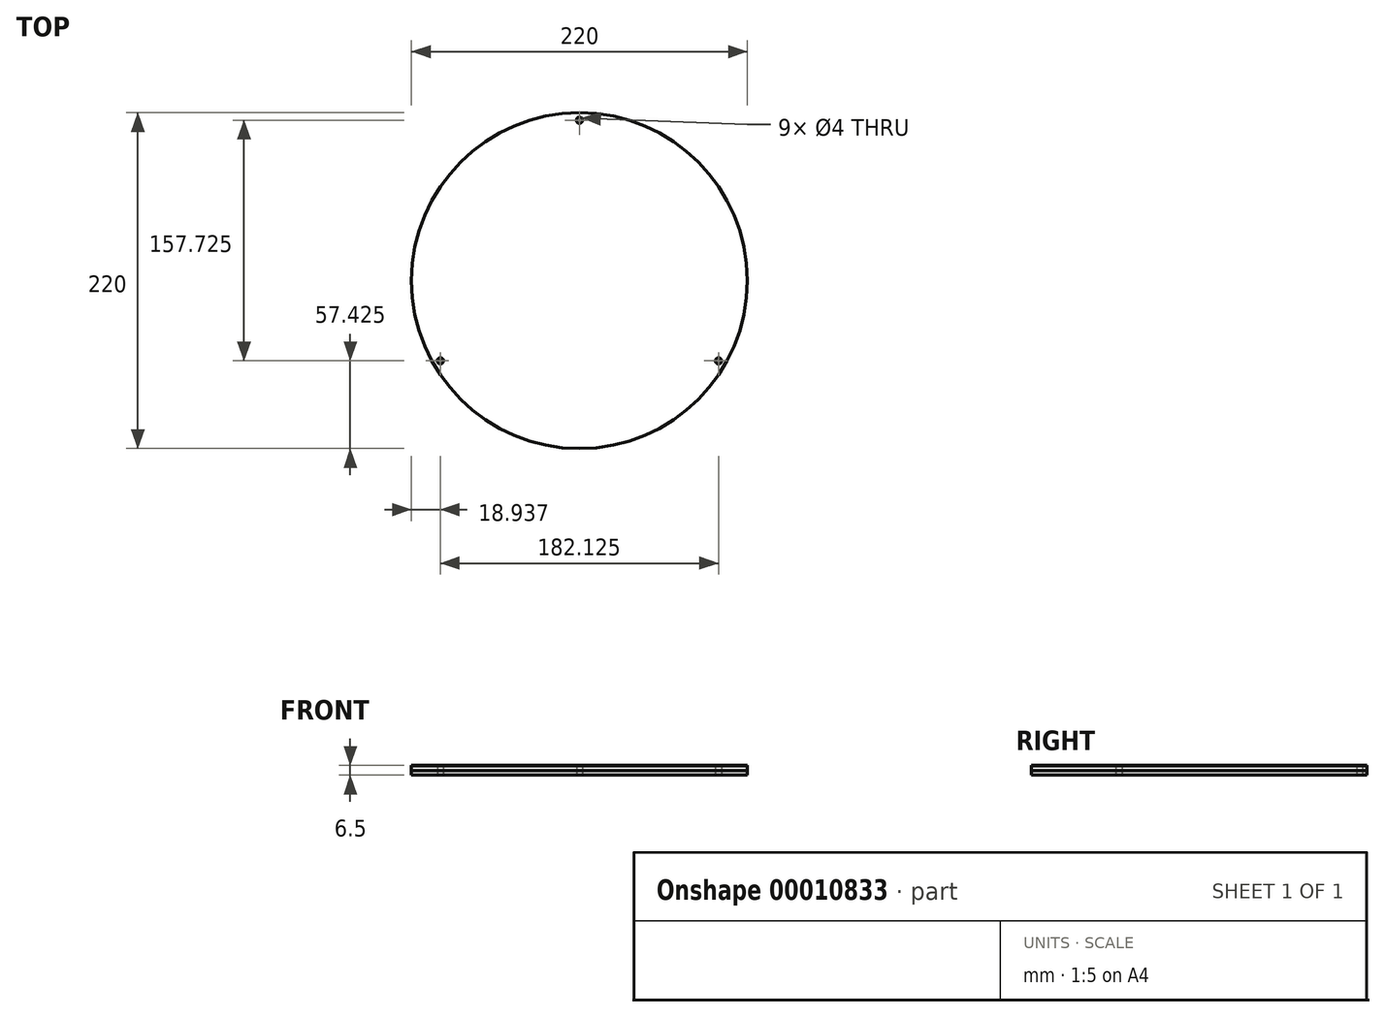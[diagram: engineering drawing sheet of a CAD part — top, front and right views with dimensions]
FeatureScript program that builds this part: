
annotation { "Feature Type Name" : "Feature", "Feature Type Description" : "" }
export const myFeature = defineFeature(function(context is Context, id is Id, definition is map)
    precondition{}
    {
        {
            var Q0;
            Q0=qCreatedBy(makeId("Top.planeOp"),FACE);
            var sketch = newSketch(context, id + "F0", { "sketchPlane" : qUnion([Q0])});
            skCircle(sketch, "E0", {"center": v(0, 0) * mm, "radius": 110 * mm});
            skCircle(sketch, "E1", {"center": v(0, 0) * mm, "radius": 105.15 * mm, "construction": true});
            skCircle(sketch, "E2", {"center": v(0, 105.15) * mm, "radius": 2 * mm});
            skCircle(sketch, "E3.1.0", {"center": v(-91.06, -52.57) * mm, "radius": 2 * mm});
            skCircle(sketch, "E3.2.0", {"center": v(91.06, -52.57) * mm, "radius": 2 * mm});
            skSolve(sketch);
        }
        {
            var Q0;
            Q0=makeQuery(id+"F0.imprint","IMPRINT",FACE,{"disambiguationData":[TD([[makeQuery(id+"F0.imprint","IMPRINT",EDGE,{"derivedFrom":sQuery(id+"F0.wireOp",EDGE,"E0")}),1.0]])]});
            extrude(context, id + "F1", {"entities" : qUnion([Q0]), "depth" : 3 * mm});
        }
        {
            var Q0;
            Q0=makeQuery(id+"F1.opExtrude","CAP_FACE",FACE,{"disambiguationData":[OSD([sQuery(id+"F0.wireOp",EDGE,"E0"),sQuery(id+"F0.wireOp",EDGE,"E2"),sQuery(id+"F0.wireOp",EDGE,"E3.1.0"),sQuery(id+"F0.wireOp",EDGE,"E3.2.0")])],"isStart":false});
            extrude(context, id + "F2", {"entities" : qUnion([Q0]), "depth" : 3 * mm});
        }
        {
            var Q0;
            Q0=makeQuery(id+"F2.opExtrude","CAP_FACE",FACE,{"disambiguationData":[OSD([sQuery(id+"F0.wireOp",EDGE,"E0"),sQuery(id+"F0.wireOp",EDGE,"E2"),sQuery(id+"F0.wireOp",EDGE,"E3.1.0"),sQuery(id+"F0.wireOp",EDGE,"E3.2.0")])],"isStart":false});
            extrude(context, id + "F3", {"entities" : qUnion([Q0]), "depth" : 0.5 * mm});
        }
    });
